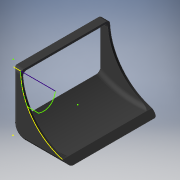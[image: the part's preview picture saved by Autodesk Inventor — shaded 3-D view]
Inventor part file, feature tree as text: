
AUTODESK INVENTOR PART (.ipt)
format: ipt  version: 2019 (Build 230136000, 136)  size: 195,072 bytes
history: native  units: in
note: dims shown in document units (in); Inventor stores cm internally (conversion verified against a paired STEP export)
features: sketch x4, extrude x3, fillet x2
ambient origin geometry x8: Origin, YZ Plane, XZ Plane, XY Plane, X Axis, Y Axis, Z Axis, Center Point
bodies: Body1 (feature_tree)
feature tree (9):
  extrude  "Extrusion5"  Depth=0.5in
  extrude  "Extrusion6"  Depth=0.5in
  fillet  "Fillet3"  Radius=3.75in
  extrude  "Extrusion7"  Depth=0.15in
  fillet  "Fillet4"  Radius=0.15in
  sketch  "Sketch7"  dims[d39=0.125in d40=0.15in d41=4.0in d42=0.0in d43=0.75in d44=5.8876in d45=4.0in d46=0.0in d47=0.25in d48=3.8339in]
  sketch  "Sketch1"  dims[d0=4.0in d14=0.5in]
  sketch  "Sketch5"  dims[d15=150.0deg d16=0.5in d28=3.75in]
  sketch  "Sketch6"  dims[d34=6.0in d35=0.0in d37=0.15in d38=0.15in]
